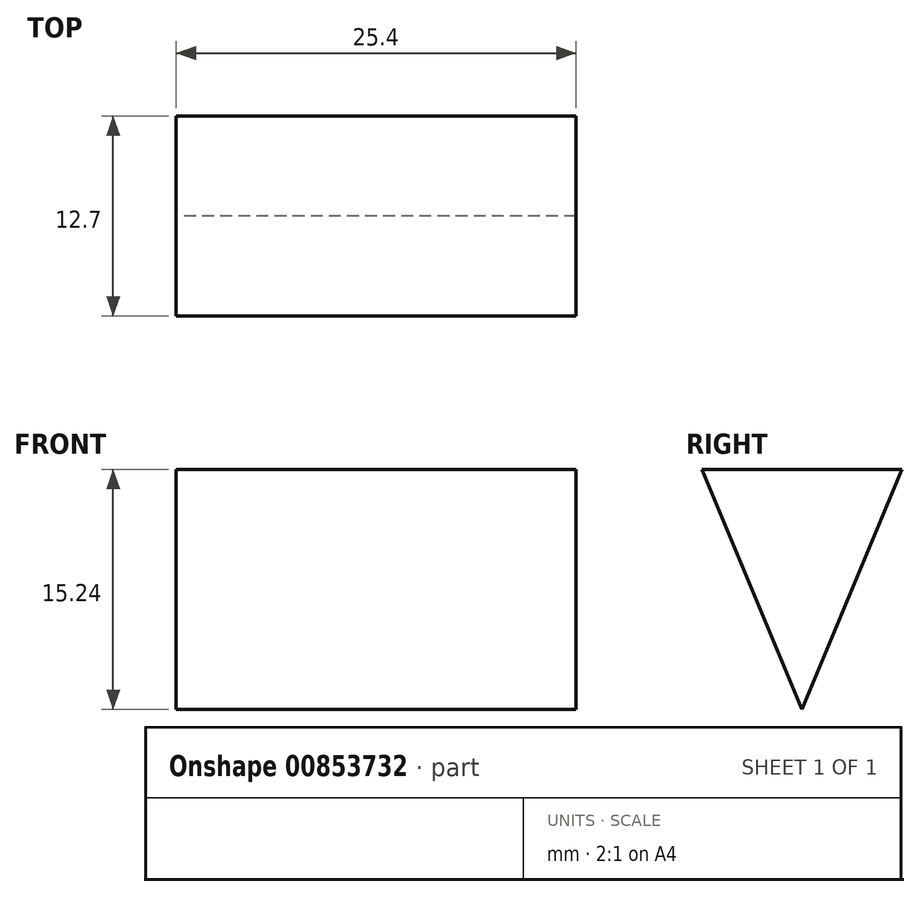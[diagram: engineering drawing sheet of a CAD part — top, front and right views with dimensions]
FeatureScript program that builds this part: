
annotation { "Feature Type Name" : "Feature", "Feature Type Description" : "" }
export const myFeature = defineFeature(function(context is Context, id is Id, definition is map)
    precondition{}
    {
        {
            var Q0;
            Q0=qCreatedBy(makeId("Right.planeOp"),FACE);
            var sketch = newSketch(context, id + "F0", { "sketchPlane" : qUnion([Q0])});
            skLineSegment(sketch, "E0", {"start": v(0, 0) * mm, "end": v(-6.35, 0) * mm});
            skLineSegment(sketch, "E1", {"start": v(0, 0) * mm, "end": v(6.35, 0) * mm});
            skLineSegment(sketch, "E2", {"start": v(-6.35, 0) * mm, "end": v(0, -15.24) * mm});
            skLineSegment(sketch, "E3", {"start": v(6.35, 0) * mm, "end": v(0, -15.24) * mm});
            skSolve(sketch);
        }
        {
            var Q0;
            Q0=makeQuery(id+"F0.imprint","IMPRINT",FACE,{"disambiguationData":[TD([[makeQuery(id+"F0.imprint","IMPRINT",EDGE,{"derivedFrom":sQuery(id+"F0.wireOp",EDGE,"E0")}),1.0]])]});
            var Q1;
            Q1=sQuery(id+"F0.wireOp",EDGE,"E0");
            var Q2;
            Q2=sQuery(id+"F0.wireOp",EDGE,"E1");
            var Q3;
            Q3=sQuery(id+"F0.wireOp",EDGE,"E3");
            var Q4;
            Q4=sQuery(id+"F0.wireOp",EDGE,"E2");
            extrude(context, id + "F1", {"entities" : qUnion([Q0]), "surfaceEntities" : qUnion([Q1, Q2, Q3, Q4]), "depth" : 12.7 * mm, "offsetDistance" : 25.4 * mm});
        }
        {
            var Q0;
            Q0=makeQuery(id+"F1.opExtrude","CAP_FACE",FACE,{"disambiguationData":[OSD([sQuery(id+"F0.wireOp",EDGE,"E0"),sQuery(id+"F0.wireOp",EDGE,"E1"),sQuery(id+"F0.wireOp",EDGE,"E2"),sQuery(id+"F0.wireOp",EDGE,"E3")])],"isStart":true});
            extrude(context, id + "F2", {"entities" : qUnion([Q0]), "operationType" : NewBodyOperationType.ADD, "depth" : 12.7 * mm, "offsetDistance" : 25.4 * mm});
        }
    });
